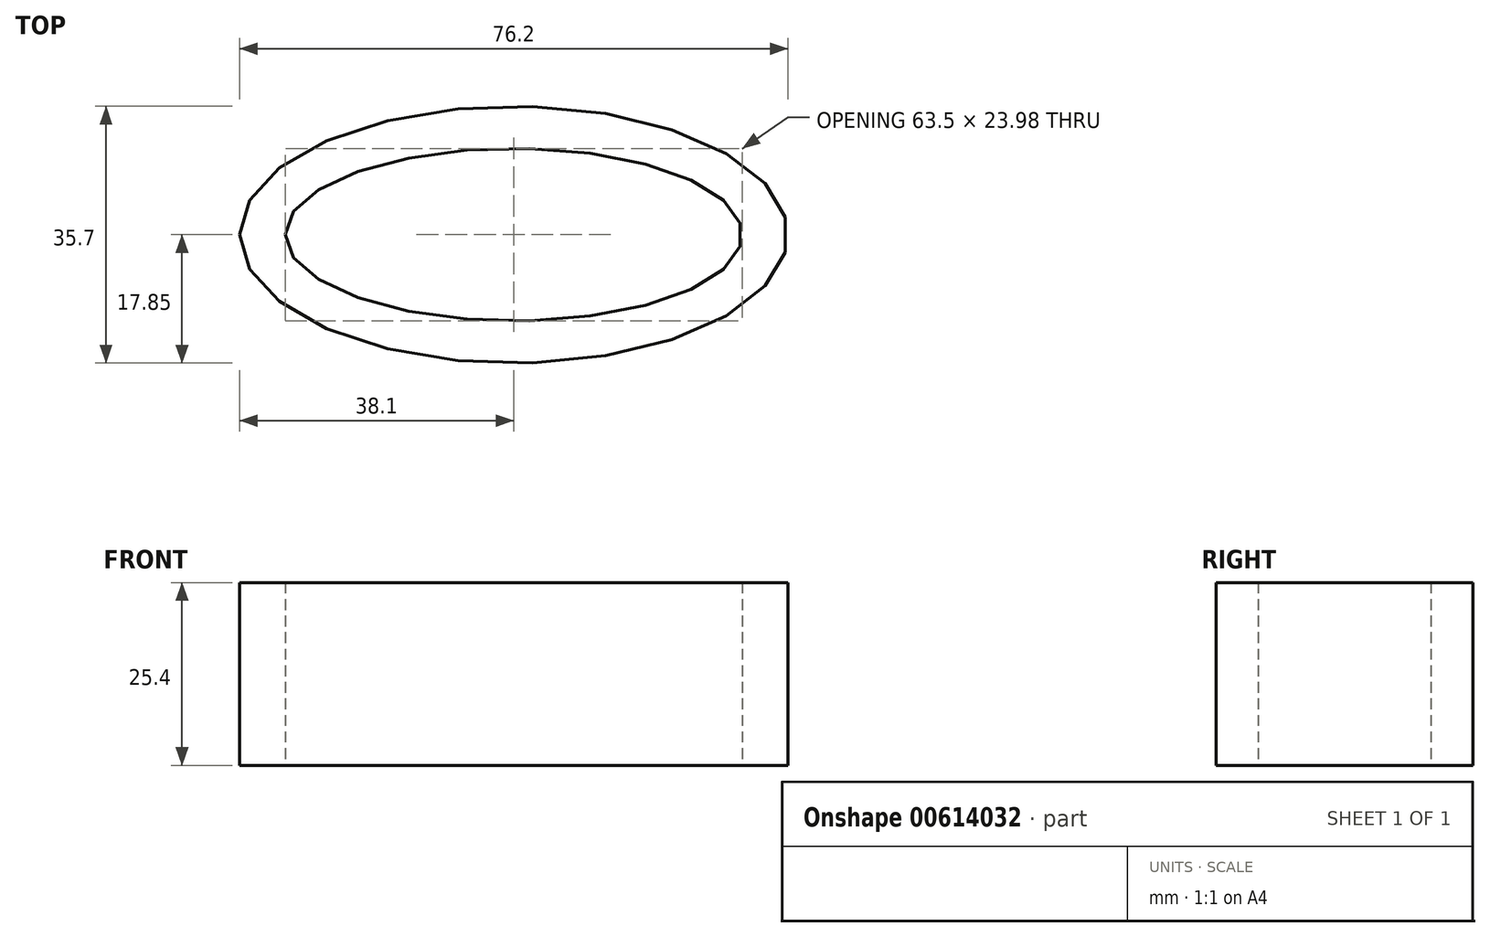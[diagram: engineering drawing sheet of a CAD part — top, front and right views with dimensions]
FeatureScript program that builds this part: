
annotation { "Feature Type Name" : "Feature", "Feature Type Description" : "" }
export const myFeature = defineFeature(function(context is Context, id is Id, definition is map)
    precondition{}
    {
        {
            var Q0;
            Q0=qCreatedBy(makeId("Top.planeOp"),FACE);
            var sketch = newSketch(context, id + "F0", { "sketchPlane" : qUnion([Q0])});
            skEllipse(sketch, "E0", {"center": v(0, 0) * mm, "majorRadius": 38.1 * mm, "minorRadius": 17.85 * mm, "majorAxis": v(-1, 0)});
            skEllipse(sketch, "E1", {"center": v(0, 0) * mm, "majorRadius": 31.75 * mm, "minorRadius": 12 * mm, "majorAxis": v(-1, 0)});
            skSolve(sketch);
        }
        {
            var Q0;
            Q0=makeQuery(id+"F0.imprint","IMPRINT",FACE,{"disambiguationData":[TD([[makeQuery(id+"F0.imprint","IMPRINT",EDGE,{"derivedFrom":sQuery(id+"F0.wireOp",EDGE,"E0")}),1.0]])]});
            extrude(context, id + "F1", {"entities" : qUnion([Q0]), "depth" : 25.4 * mm, "offsetDistance" : 25.4 * mm});
        }
    });
